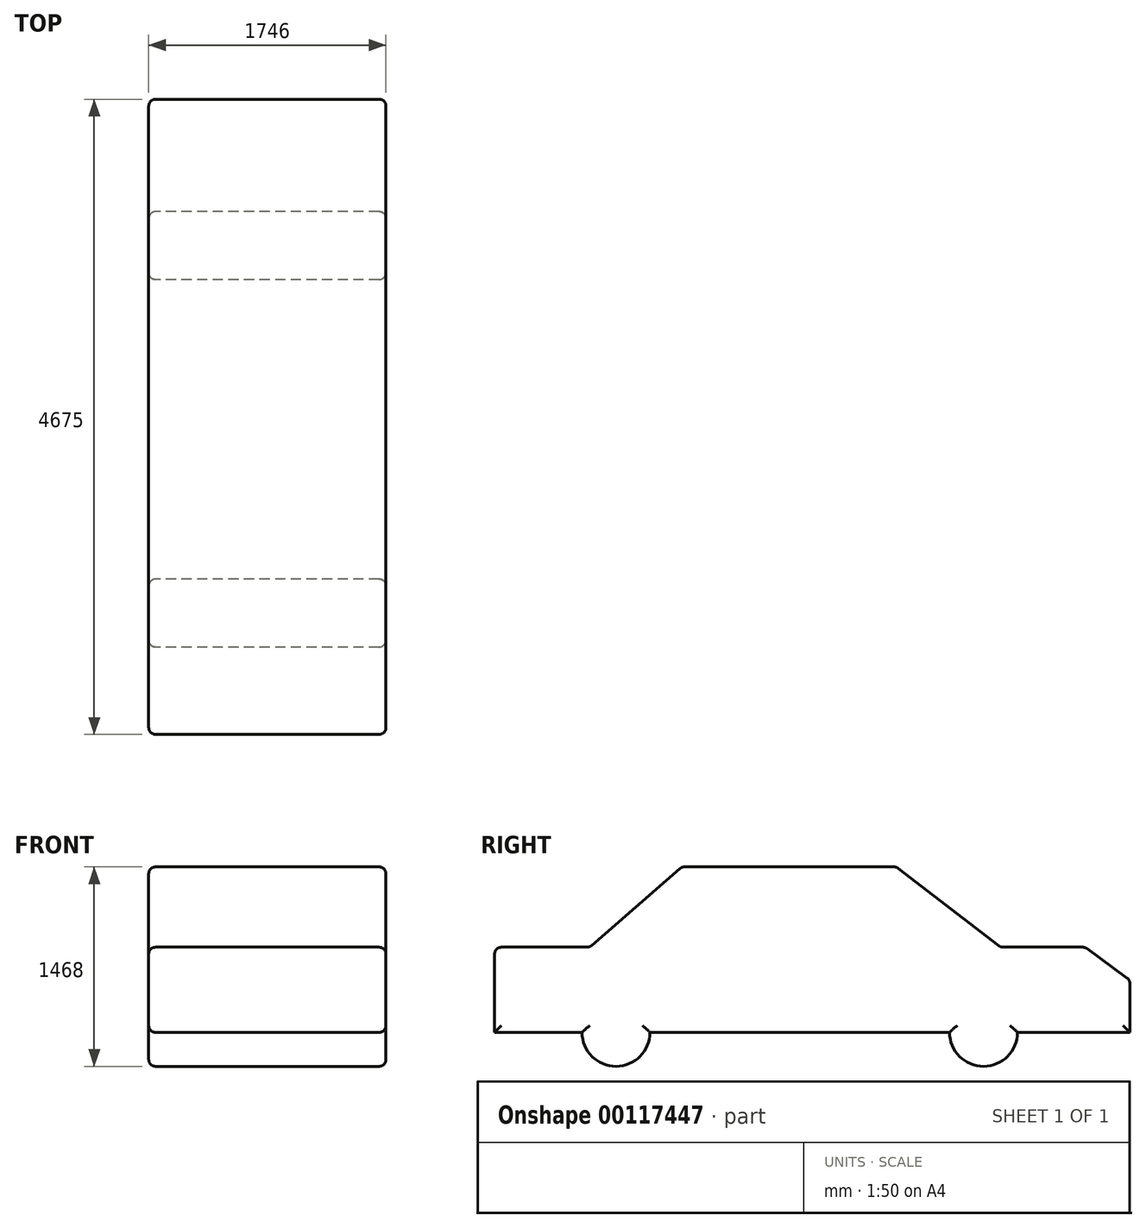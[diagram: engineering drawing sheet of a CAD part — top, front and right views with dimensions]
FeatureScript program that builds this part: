
annotation { "Feature Type Name" : "Feature", "Feature Type Description" : "" }
export const myFeature = defineFeature(function(context is Context, id is Id, definition is map)
    precondition{}
    {
        {
            var Q0;
            Q0=qCreatedBy(makeId("Right.planeOp"),FACE);
            var sketch = newSketch(context, id + "F0", { "sketchPlane" : qUnion([Q0])});
            skLineSegment(sketch, "E0", {"start": v(-250, 0) * mm, "end": v(-893.32, 0) * mm});
            skLineSegment(sketch, "E1", {"start": v(-893.32, 0) * mm, "end": v(-893.32, 626.76) * mm});
            skLineSegment(sketch, "E2", {"start": v(-893.32, 626.76) * mm, "end": v(-194.2, 626.76) * mm});
            skLineSegment(sketch, "E3", {"start": v(-194.2, 626.76) * mm, "end": v(485.73, 1218) * mm});
            skLineSegment(sketch, "E4", {"start": v(485.73, 1218) * mm, "end": v(2063.5, 1218) * mm});
            skLineSegment(sketch, "E5", {"start": v(2063.5, 1218) * mm, "end": v(2832.07, 626.76) * mm});
            skLineSegment(sketch, "E6", {"start": v(2832.07, 626.76) * mm, "end": v(3450.93, 626.76) * mm});
            skLineSegment(sketch, "E7", {"start": v(3450.93, 626.76) * mm, "end": v(3781.68, 386.2) * mm});
            skLineSegment(sketch, "E8", {"start": v(3781.68, 386.2) * mm, "end": v(3781.68, 0) * mm});
            skLineSegment(sketch, "E9", {"start": v(3781.68, 0) * mm, "end": v(2955, 0) * mm});
            skArc(sketch, "E10", {"start": v(-250, 0) * mm, "mid": v(0, -250) * mm, "end": v(250, 0) * mm});
            skArc(sketch, "E11", {"start": v(2455, 0) * mm, "mid": v(2705, -250) * mm, "end": v(2955, 0) * mm});
            skLineSegment(sketch, "E12", {"start": v(250, 0) * mm, "end": v(2455, 0) * mm});
            skSolve(sketch);
        }
        {
            var Q0;
            Q0 = qSketchRegion(id + "F0", true);
            extrude(context, id + "F1", {"entities" : qUnion([Q0]), "depth" : 1746 * mm});
        }
        {
            var Q0;
            Q0=makeQuery(id+"F1.opExtrude","CAP_FACE",FACE,{"disambiguationData":[OSD([sQuery(id+"F0.wireOp",EDGE,"E0"),sQuery(id+"F0.wireOp",EDGE,"E1"),sQuery(id+"F0.wireOp",EDGE,"E2"),sQuery(id+"F0.wireOp",EDGE,"E3"),sQuery(id+"F0.wireOp",EDGE,"E4"),sQuery(id+"F0.wireOp",EDGE,"E5"),sQuery(id+"F0.wireOp",EDGE,"E6"),sQuery(id+"F0.wireOp",EDGE,"E7"),sQuery(id+"F0.wireOp",EDGE,"E8"),sQuery(id+"F0.wireOp",EDGE,"E9"),sQuery(id+"F0.wireOp",EDGE,"E10"),sQuery(id+"F0.wireOp",EDGE,"E11"),sQuery(id+"F0.wireOp",EDGE,"E12")])],"isStart":false});
            var Q1;
            Q1=makeQuery(id+"F1.opExtrude","CAP_FACE",FACE,{"disambiguationData":[OSD([sQuery(id+"F0.wireOp",EDGE,"E0"),sQuery(id+"F0.wireOp",EDGE,"E1"),sQuery(id+"F0.wireOp",EDGE,"E2"),sQuery(id+"F0.wireOp",EDGE,"E3"),sQuery(id+"F0.wireOp",EDGE,"E4"),sQuery(id+"F0.wireOp",EDGE,"E5"),sQuery(id+"F0.wireOp",EDGE,"E6"),sQuery(id+"F0.wireOp",EDGE,"E7"),sQuery(id+"F0.wireOp",EDGE,"E8"),sQuery(id+"F0.wireOp",EDGE,"E9"),sQuery(id+"F0.wireOp",EDGE,"E10"),sQuery(id+"F0.wireOp",EDGE,"E11"),sQuery(id+"F0.wireOp",EDGE,"E12")])],"isStart":true});
            var Q2;
            Q2=makeQuery(id+"F1.opExtrude","SWEPT_FACE",FACE,{"disambiguationData":[OSD([sQuery(id+"F0.wireOp",EDGE,"E3")])]});
            var Q3;
            Q3=makeQuery(id+"F1.opExtrude","SWEPT_FACE",FACE,{"disambiguationData":[OSD([sQuery(id+"F0.wireOp",EDGE,"E5")])]});
            var Q4;
            Q4=makeQuery(id+"F1.opExtrude","SWEPT_FACE",FACE,{"disambiguationData":[OSD([sQuery(id+"F0.wireOp",EDGE,"E7")])]});
            var Q5;
            Q5=makeQuery(id+"F1.opExtrude","SWEPT_EDGE",EDGE,{"disambiguationData":[OSD([sQuery(id+"F0.wireOp",EDGE,"E1"),sQuery(id+"F0.wireOp",EDGE,"E2")])]});
            fillet(context, id + "F2", {"entities" : qUnion([Q0, Q1, Q2, Q3, Q4, Q5]), "radius" : 50 * mm, "tangentPropagation" : true, "allowEdgeOverflow" : false});
        }
    });
